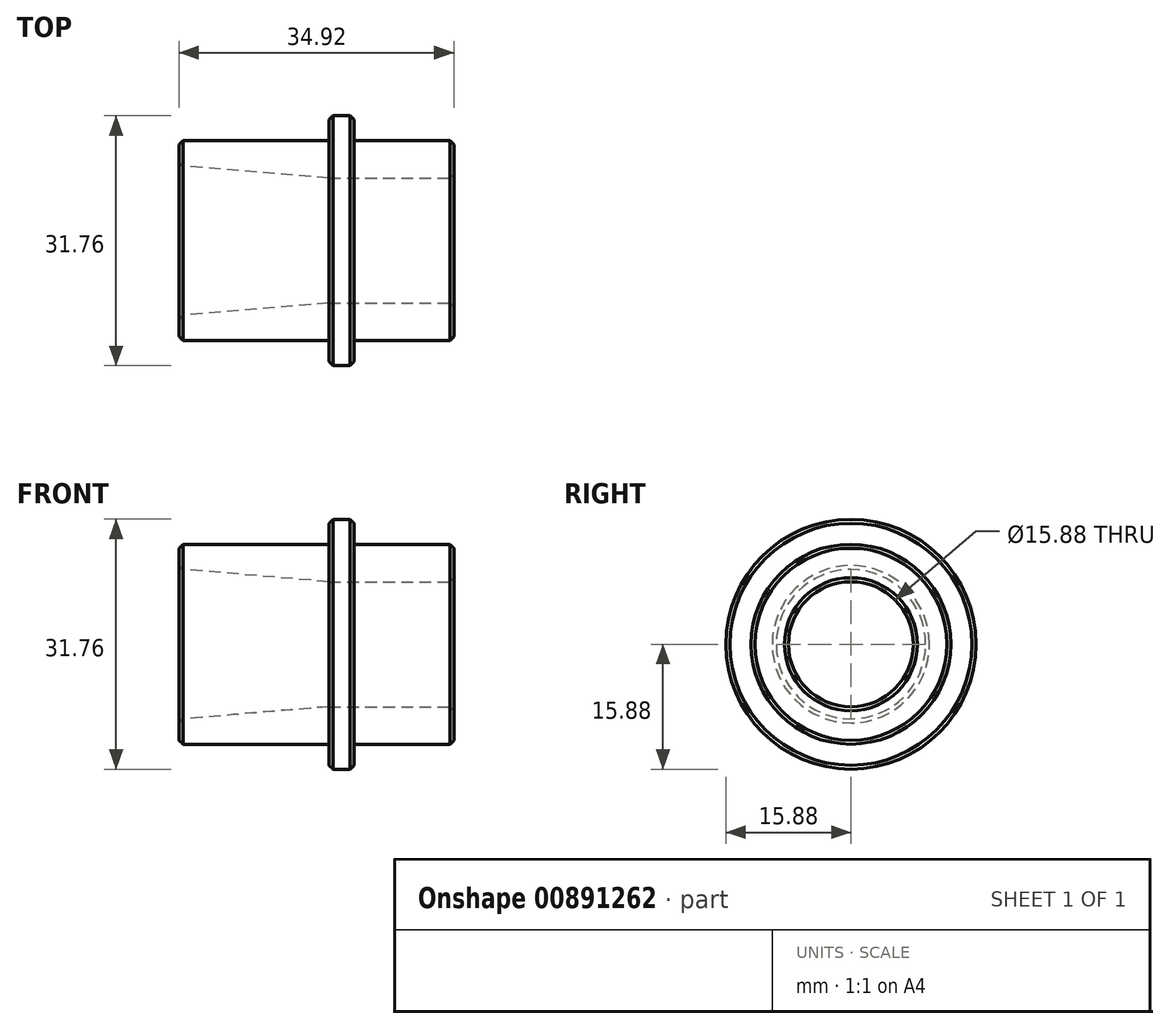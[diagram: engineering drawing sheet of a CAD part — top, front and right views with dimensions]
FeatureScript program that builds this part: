
annotation { "Feature Type Name" : "Feature", "Feature Type Description" : "" }
export const myFeature = defineFeature(function(context is Context, id is Id, definition is map)
    precondition{}
    {
        {
            var Q0;
            Q0=qCreatedBy(makeId("Front.planeOp"),FACE);
            var sketch = newSketch(context, id + "F0", { "sketchPlane" : qUnion([Q0])});
            skLineSegment(sketch, "E0", {"start": v(-41.56, 12.7) * mm, "end": v(-22.51, 12.7) * mm});
            skLineSegment(sketch, "E1", {"start": v(-22.51, 12.7) * mm, "end": v(-22.51, 15.88) * mm});
            skLineSegment(sketch, "E2", {"start": v(-22.51, 15.88) * mm, "end": v(-19.34, 15.88) * mm});
            skLineSegment(sketch, "E3", {"start": v(-19.34, 15.88) * mm, "end": v(-19.34, 12.7) * mm});
            skLineSegment(sketch, "E4", {"start": v(-19.34, 12.7) * mm, "end": v(-6.64, 12.7) * mm});
            skLineSegment(sketch, "E5", {"start": v(-6.64, 12.7) * mm, "end": v(-6.64, 7.94) * mm});
            skLineSegment(sketch, "E6", {"start": v(-6.64, 7.94) * mm, "end": v(-22.51, 7.94) * mm});
            skLineSegment(sketch, "E7", {"start": v(-22.51, 7.94) * mm, "end": v(-41.56, 9.52) * mm});
            skLineSegment(sketch, "E8", {"start": v(-41.56, 9.52) * mm, "end": v(-41.56, 12.7) * mm});
            skLineSegment(sketch, "E9", {"start": v(0, 0) * mm, "end": v(-45.48, 0) * mm});
            skSolve(sketch);
        }
        {
            var Q0;
            Q0=makeQuery(id+"F0.imprint","IMPRINT",FACE,{"disambiguationData":[TD([[makeQuery(id+"F0.imprint","IMPRINT",EDGE,{"derivedFrom":sQuery(id+"F0.wireOp",EDGE,"E0")}),-1.0]])]});
            var Q1;
            Q1=sQuery(id+"F0.wireOp",EDGE,"E9");
            revolve(context, id + "F1", {"surfaceOperationType" : NewSurfaceOperationType.NEW, "entities" : qUnion([Q0]), "axis" : qUnion([Q1]), "revolveType" : RevolveType.FULL});
        }
        {
            var Q0;
            Q0=makeQuery(id+"F1.opRevolve","SWEPT_EDGE",EDGE,{"disambiguationData":[OSD([sQuery(id+"F0.wireOp",EDGE,"E1"),sQuery(id+"F0.wireOp",EDGE,"E2")])]});
            var Q1;
            Q1=makeQuery(id+"F1.opRevolve","SWEPT_EDGE",EDGE,{"disambiguationData":[OSD([sQuery(id+"F0.wireOp",EDGE,"E2"),sQuery(id+"F0.wireOp",EDGE,"E3")])]});
            var Q2;
            Q2=makeQuery(id+"F1.opRevolve","SWEPT_EDGE",EDGE,{"disambiguationData":[OSD([sQuery(id+"F0.wireOp",EDGE,"E0"),sQuery(id+"F0.wireOp",EDGE,"E8")])]});
            var Q3;
            Q3=makeQuery(id+"F1.opRevolve","SWEPT_EDGE",EDGE,{"disambiguationData":[OSD([sQuery(id+"F0.wireOp",EDGE,"E4"),sQuery(id+"F0.wireOp",EDGE,"E5")])]});
            var Q4;
            Q4=makeQuery(id+"F1.opRevolve","SWEPT_EDGE",EDGE,{"disambiguationData":[OSD([sQuery(id+"F0.wireOp",EDGE,"E7"),sQuery(id+"F0.wireOp",EDGE,"E8")])]});
            var Q5;
            Q5=makeQuery(id+"F1.opRevolve","SWEPT_EDGE",EDGE,{"disambiguationData":[OSD([sQuery(id+"F0.wireOp",EDGE,"E5"),sQuery(id+"F0.wireOp",EDGE,"E6")])]});
            chamfer(context, id + "F2", {"entities" : qUnion([Q0, Q1, Q2, Q3, Q4, Q5]), "width" : 0.5 * mm, "tangentPropagation" : true});
        }
    });
